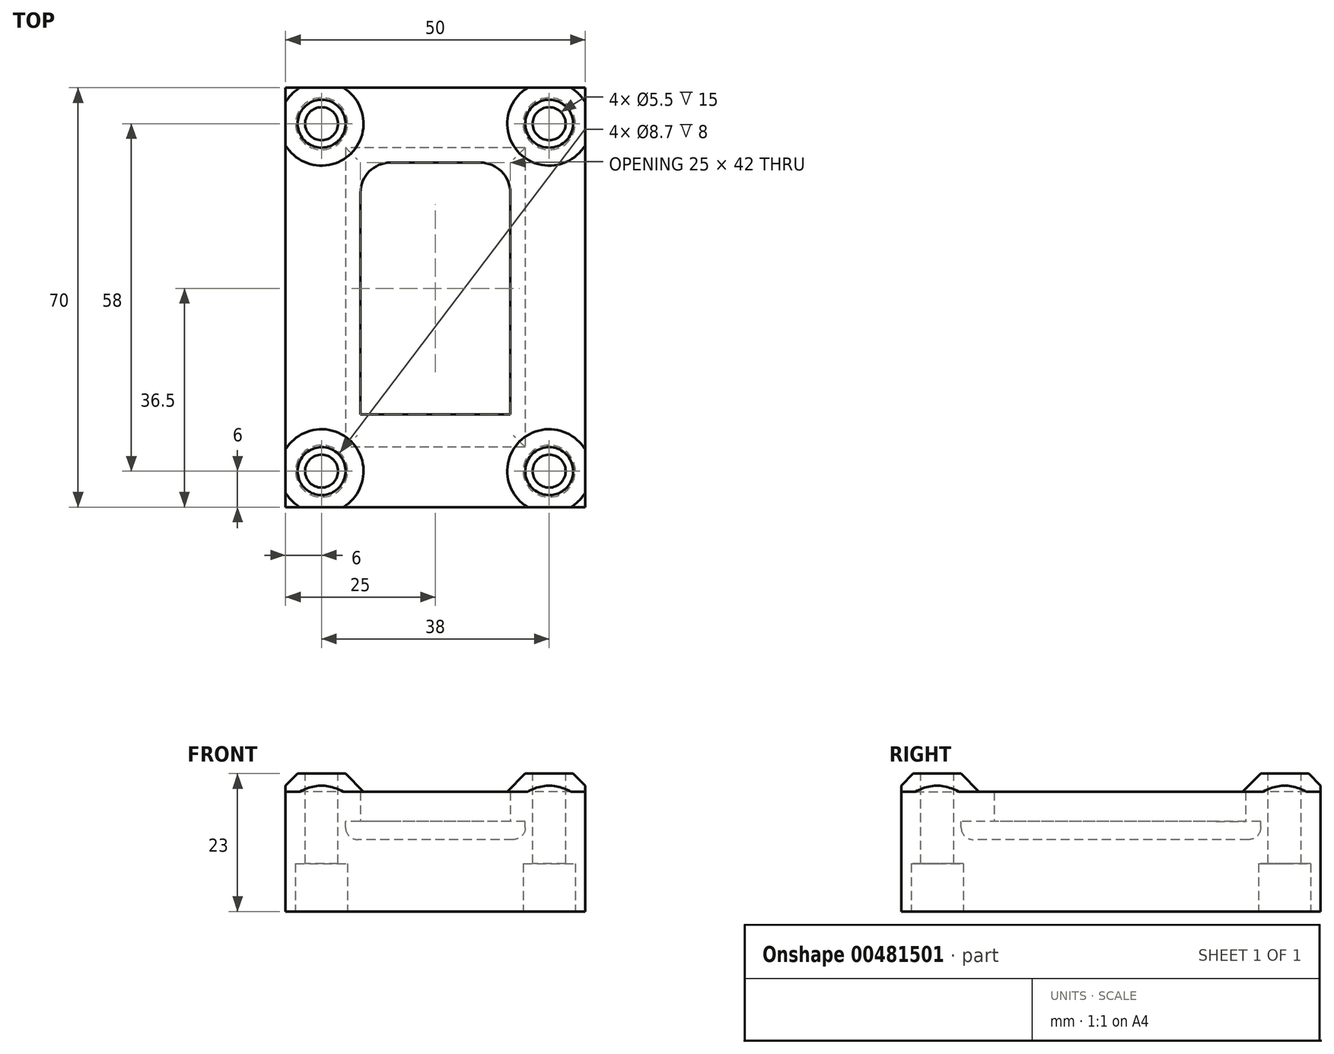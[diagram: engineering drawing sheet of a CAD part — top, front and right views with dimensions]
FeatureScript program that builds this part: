
annotation { "Feature Type Name" : "Feature", "Feature Type Description" : "" }
export const myFeature = defineFeature(function(context is Context, id is Id, definition is map)
    precondition{}
    {
        {
            var Q0;
            Q0=qCreatedBy(makeId("Top.planeOp"),FACE);
            var sketch = newSketch(context, id + "F0", { "sketchPlane" : qUnion([Q0])});
            skLineSegment(sketch, "E0.bottom", {"start": v(15, 25) * mm, "end": v(-15, 25) * mm});
            skLineSegment(sketch, "E0.top", {"start": v(15, -25) * mm, "end": v(-15, -25) * mm});
            skLineSegment(sketch, "E0.left", {"start": v(15, 25) * mm, "end": v(15, -25) * mm});
            skLineSegment(sketch, "E0.right", {"start": v(-15, 25) * mm, "end": v(-15, -25) * mm});
            skPoint(sketch, "E0.middle", {"position": v(0, 0) * mm});
            skLineSegment(sketch, "E1.bottom", {"start": v(25, 35) * mm, "end": v(-25, 35) * mm});
            skLineSegment(sketch, "E1.top", {"start": v(25, -35) * mm, "end": v(-25, -35) * mm});
            skLineSegment(sketch, "E1.left", {"start": v(25, 35) * mm, "end": v(25, -35) * mm});
            skLineSegment(sketch, "E1.right", {"start": v(-25, 35) * mm, "end": v(-25, -35) * mm});
            skLineSegment(sketch, "E2", {"start": v(-19, 35) * mm, "end": v(-19, 29) * mm});
            skCircle(sketch, "E3", {"center": v(-19, 29) * mm, "radius": 2.75 * mm});
            skLineSegment(sketch, "E4", {"start": v(-19, -35) * mm, "end": v(-19, -29) * mm});
            skLineSegment(sketch, "E5", {"start": v(-19, -29) * mm, "end": v(-25, -29) * mm});
            skCircle(sketch, "E6", {"center": v(-19, -29) * mm, "radius": 2.75 * mm});
            skLineSegment(sketch, "E7", {"start": v(25, -29) * mm, "end": v(19, -29) * mm});
            skCircle(sketch, "E8", {"center": v(19, -29) * mm, "radius": 2.75 * mm});
            skLineSegment(sketch, "E9", {"start": v(19, -29) * mm, "end": v(19, -35) * mm});
            skLineSegment(sketch, "E10", {"start": v(19, 35) * mm, "end": v(19, 29) * mm});
            skLineSegment(sketch, "E11", {"start": v(19, 29) * mm, "end": v(25, 29) * mm});
            skCircle(sketch, "E12", {"center": v(19, 29) * mm, "radius": 2.75 * mm});
            skSolve(sketch);
        }
        {
            var Q0;
            Q0=makeQuery(id+"F0.imprint","IMPRINT",FACE,{"disambiguationData":[TD([[makeQuery(id+"F0.imprint","IMPRINT",EDGE,{"derivedFrom":sQuery(id+"F0.wireOp",EDGE,"E0.bottom")}),-1.0]])]});
            var Q1;
            {var subQ1=sQuery(id+"F0.wireOp",EDGE,"E1.left");var subQ6=sQuery(id+"F0.wireOp",EDGE,"E1.bottom");var subQ9=makeQuery(id+"F0.imprint","INTERSECT",VERTEX,{"derivedFrom":[subQ6,subQ1]});Q1=makeQuery(id+"F0.imprint","IMPRINT",FACE,{"disambiguationData":[TD([[makeQuery(id+"F0.imprint","IMPRINT",EDGE,{"disambiguationData":[TD([[subQ9,-1.0]])],"derivedFrom":subQ6}),1.0]])]});}
            var Q2;
            {var subQ5=sQuery(id+"F0.wireOp",EDGE,"E1.left");var subQ7=sQuery(id+"F0.wireOp",EDGE,"E1.top");var subQ8=makeQuery(id+"F0.imprint","INTERSECT",VERTEX,{"derivedFrom":[subQ7,subQ5]});Q2=makeQuery(id+"F0.imprint","IMPRINT",FACE,{"disambiguationData":[TD([[makeQuery(id+"F0.imprint","IMPRINT",EDGE,{"disambiguationData":[TD([[subQ8,-1.0]])],"derivedFrom":subQ7}),-1.0]])]});}
            var Q3;
            {var subQ1=sQuery(id+"F0.wireOp",EDGE,"E1.top");var subQ6=sQuery(id+"F0.wireOp",EDGE,"E1.right");var subQ9=makeQuery(id+"F0.imprint","INTERSECT",VERTEX,{"derivedFrom":[subQ1,subQ6]});Q3=makeQuery(id+"F0.imprint","IMPRINT",FACE,{"disambiguationData":[TD([[makeQuery(id+"F0.imprint","IMPRINT",EDGE,{"disambiguationData":[TD([[subQ9,1.0]])],"derivedFrom":subQ1}),-1.0]])]});}
            var Q4;
            Q4=makeQuery(id+"F0.imprint","IMPRINT",FACE,{"disambiguationData":[TD([[makeQuery(id+"F0.imprint","IMPRINT",EDGE,{"derivedFrom":sQuery(id+"F0.wireOp",EDGE,"E0.bottom")}),1.0]])]});
            extrude(context, id + "F1", {"entities" : qUnion([Q0, Q1, Q2, Q3, Q4]), "oppositeDirection" : true, "depth" : 15 * mm});
        }
        {
            var Q0;
            Q0=makeQuery(id+"F1.opExtrude","CAP_FACE",FACE,{"disambiguationData":[OSD([sQuery(id+"F0.wireOp",EDGE,"E1.bottom"),sQuery(id+"F0.wireOp",EDGE,"E1.top"),sQuery(id+"F0.wireOp",EDGE,"E1.left"),sQuery(id+"F0.wireOp",EDGE,"E1.right"),sQuery(id+"F0.wireOp",EDGE,"E3"),sQuery(id+"F0.wireOp",EDGE,"E6"),sQuery(id+"F0.wireOp",EDGE,"E8"),sQuery(id+"F0.wireOp",EDGE,"E12")])],"isStart":false});
            var sketch = newSketch(context, id + "F2", { "sketchPlane" : qUnion([Q0])});
            skCircle(sketch, "E13", {"center": v(-19, 29) * mm, "radius": 4.35 * mm});
            skCircle(sketch, "E14", {"center": v(-19, -29) * mm, "radius": 4.35 * mm});
            skCircle(sketch, "E15", {"center": v(19, -29) * mm, "radius": 4.35 * mm});
            skCircle(sketch, "E16", {"center": v(19, 29) * mm, "radius": 4.35 * mm});
            skSolve(sketch);
        }
        {
            var Q0;
            Q0=makeQuery(id+"F2.imprint","IMPRINT",FACE,{"disambiguationData":[TD([[makeQuery(id+"F2.imprint","IMPRINT",EDGE,{"derivedFrom":sQuery(id+"F2.wireOp",EDGE,"E13")}),1.0]])]});
            var Q1;
            Q1=makeQuery(id+"F2.imprint","IMPRINT",FACE,{"disambiguationData":[TD([[makeQuery(id+"F2.imprint","IMPRINT",EDGE,{"derivedFrom":sQuery(id+"F2.wireOp",EDGE,"E16")}),1.0]])]});
            var Q2;
            Q2=makeQuery(id+"F2.imprint","IMPRINT",FACE,{"disambiguationData":[TD([[makeQuery(id+"F2.imprint","IMPRINT",EDGE,{"derivedFrom":sQuery(id+"F2.wireOp",EDGE,"E15")}),1.0]])]});
            var Q3;
            Q3=makeQuery(id+"F2.imprint","IMPRINT",FACE,{"disambiguationData":[TD([[makeQuery(id+"F2.imprint","IMPRINT",EDGE,{"derivedFrom":sQuery(id+"F2.wireOp",EDGE,"E14")}),1.0]])]});
            extrude(context, id + "F3", {"entities" : qUnion([Q0, Q1, Q2, Q3]), "operationType" : NewBodyOperationType.REMOVE, "oppositeDirection" : true, "depth" : 8 * mm});
        }
        {
            var Q0;
            Q0=makeQuery(id+"F0.imprint","IMPRINT",FACE,{"disambiguationData":[TD([[makeQuery(id+"F0.imprint","IMPRINT",EDGE,{"derivedFrom":sQuery(id+"F0.wireOp",EDGE,"E0.bottom")}),1.0]])]});
            extrude(context, id + "F4", {"entities" : qUnion([Q0]), "operationType" : NewBodyOperationType.REMOVE, "oppositeDirection" : true, "depth" : 3 * mm});
        }
        {
            var Q0;
            Q0=makeQuery(id+"F4.boolean.opBoolean","COPY",EDGE,{"derivedFrom":makeQuery(id+"F4.opExtrude","CAP_EDGE",EDGE,{"disambiguationData":[OSD([sQuery(id+"F0.wireOp",EDGE,"E0.bottom")])],"isStart":false})});
            var Q1;
            Q1=makeQuery(id+"F4.boolean.opBoolean","COPY",EDGE,{"derivedFrom":makeQuery(id+"F4.opExtrude","CAP_EDGE",EDGE,{"disambiguationData":[OSD([sQuery(id+"F0.wireOp",EDGE,"E0.left")])],"isStart":false})});
            var Q2;
            Q2=makeQuery(id+"F4.boolean.opBoolean","COPY",EDGE,{"derivedFrom":makeQuery(id+"F4.opExtrude","CAP_EDGE",EDGE,{"disambiguationData":[OSD([sQuery(id+"F0.wireOp",EDGE,"E0.right")])],"isStart":false})});
            var Q3;
            Q3=makeQuery(id+"F4.boolean.opBoolean","COPY",EDGE,{"derivedFrom":makeQuery(id+"F4.opExtrude","CAP_EDGE",EDGE,{"disambiguationData":[OSD([sQuery(id+"F0.wireOp",EDGE,"E0.top")])],"isStart":false})});
            fillet(context, id + "F5", {"entities" : qUnion([Q0, Q1, Q2, Q3]), "radius" : 2 * mm, "tangentPropagation" : true, "allowEdgeOverflow" : false});
        }
        {
            var Q0;
            Q0=makeQuery(id+"F1.opExtrude","CAP_FACE",FACE,{"disambiguationData":[OSD([sQuery(id+"F0.wireOp",EDGE,"E1.bottom"),sQuery(id+"F0.wireOp",EDGE,"E1.top"),sQuery(id+"F0.wireOp",EDGE,"E1.left"),sQuery(id+"F0.wireOp",EDGE,"E1.right"),sQuery(id+"F0.wireOp",EDGE,"E3"),sQuery(id+"F0.wireOp",EDGE,"E6"),sQuery(id+"F0.wireOp",EDGE,"E8"),sQuery(id+"F0.wireOp",EDGE,"E12")])],"isStart":true});
            var sketch = newSketch(context, id + "F6", { "sketchPlane" : qUnion([Q0])});
            skLineSegment(sketch, "E17.bottom", {"start": v(12.5, 22.5) * mm, "end": v(-12.5, 22.5) * mm});
            skLineSegment(sketch, "E17.top", {"start": v(12.5, -22.5) * mm, "end": v(-12.5, -22.5) * mm});
            skLineSegment(sketch, "E17.left", {"start": v(12.5, 22.5) * mm, "end": v(12.5, -22.5) * mm});
            skLineSegment(sketch, "E17.right", {"start": v(-12.5, 22.5) * mm, "end": v(-12.5, -22.5) * mm});
            skPoint(sketch, "E17.middle", {"position": v(0, 0) * mm});
            skLineSegment(sketch, "E18.bottom", {"start": v(25, 35) * mm, "end": v(-25, 35) * mm});
            skLineSegment(sketch, "E18.top", {"start": v(25, -35) * mm, "end": v(-25, -35) * mm});
            skLineSegment(sketch, "E18.left", {"start": v(25, 35) * mm, "end": v(25, -35) * mm});
            skLineSegment(sketch, "E18.right", {"start": v(-25, 35) * mm, "end": v(-25, -35) * mm});
            skCircle(sketch, "E19", {"center": v(19, -29) * mm, "radius": 2.75 * mm});
            skCircle(sketch, "E20", {"center": v(19, 29) * mm, "radius": 2.75 * mm});
            skCircle(sketch, "E21", {"center": v(-19, 29) * mm, "radius": 2.75 * mm});
            skCircle(sketch, "E22", {"center": v(-19, -29) * mm, "radius": 2.75 * mm});
            skCircle(sketch, "E23", {"center": v(-19, -29) * mm, "radius": 4 * mm});
            skCircle(sketch, "E24", {"center": v(19, -29) * mm, "radius": 4 * mm});
            skCircle(sketch, "E25", {"center": v(19, 29) * mm, "radius": 4 * mm});
            skCircle(sketch, "E26", {"center": v(-19, 29) * mm, "radius": 4 * mm});
            skSolve(sketch);
        }
        {
            var Q0;
            Q0=makeQuery(id+"F6.imprint","IMPRINT",FACE,{"disambiguationData":[TD([[makeQuery(id+"F6.imprint","IMPRINT",EDGE,{"derivedFrom":sQuery(id+"F6.wireOp",EDGE,"E18.bottom")}),1.0]])]});
            var Q1;
            Q1=makeQuery(id+"F6.imprint","IMPRINT",FACE,{"disambiguationData":[TD([[makeQuery(id+"F6.imprint","IMPRINT",EDGE,{"derivedFrom":sQuery(id+"F6.wireOp",EDGE,"E17.bottom")}),-1.0]])]});
            var Q2;
            Q2=makeQuery(id+"F6.imprint","IMPRINT",FACE,{"disambiguationData":[TD([[makeQuery(id+"F6.imprint","IMPRINT",EDGE,{"derivedFrom":sQuery(id+"F6.wireOp",EDGE,"E19")}),-1.0]])]});
            var Q3;
            Q3=makeQuery(id+"F6.imprint","IMPRINT",FACE,{"disambiguationData":[TD([[makeQuery(id+"F6.imprint","IMPRINT",EDGE,{"derivedFrom":sQuery(id+"F6.wireOp",EDGE,"E22")}),-1.0]])]});
            var Q4;
            Q4=makeQuery(id+"F6.imprint","IMPRINT",FACE,{"disambiguationData":[TD([[makeQuery(id+"F6.imprint","IMPRINT",EDGE,{"derivedFrom":sQuery(id+"F6.wireOp",EDGE,"E20")}),-1.0]])]});
            var Q5;
            Q5=makeQuery(id+"F6.imprint","IMPRINT",FACE,{"disambiguationData":[TD([[makeQuery(id+"F6.imprint","IMPRINT",EDGE,{"derivedFrom":sQuery(id+"F6.wireOp",EDGE,"E21")}),-1.0]])]});
            extrude(context, id + "F7", {"entities" : qUnion([Q0, Q1, Q2, Q3, Q4, Q5]), "depth" : 5 * mm});
        }
        {
            var Q0;
            Q0=makeQuery(id+"F6.imprint","IMPRINT",FACE,{"disambiguationData":[TD([[makeQuery(id+"F6.imprint","IMPRINT",EDGE,{"derivedFrom":sQuery(id+"F6.wireOp",EDGE,"E20")}),-1.0]])]});
            var Q1;
            Q1=makeQuery(id+"F6.imprint","IMPRINT",FACE,{"disambiguationData":[TD([[makeQuery(id+"F6.imprint","IMPRINT",EDGE,{"derivedFrom":sQuery(id+"F6.wireOp",EDGE,"E21")}),-1.0]])]});
            var Q2;
            Q2=makeQuery(id+"F6.imprint","IMPRINT",FACE,{"disambiguationData":[TD([[makeQuery(id+"F6.imprint","IMPRINT",EDGE,{"derivedFrom":sQuery(id+"F6.wireOp",EDGE,"E22")}),-1.0]])]});
            var Q3;
            Q3=makeQuery(id+"F6.imprint","IMPRINT",FACE,{"disambiguationData":[TD([[makeQuery(id+"F6.imprint","IMPRINT",EDGE,{"derivedFrom":sQuery(id+"F6.wireOp",EDGE,"E19")}),-1.0]])]});
            extrude(context, id + "F8", {"entities" : qUnion([Q0, Q1, Q2, Q3]), "operationType" : NewBodyOperationType.ADD, "depth" : 8 * mm});
        }
        {
            var Q0;
            Q0=makeQuery(id+"F7.opExtrude","SWEPT_FACE",FACE,{"disambiguationData":[OSD([sQuery(id+"F6.wireOp",EDGE,"E17.top")])]});
            extrude(context, id + "F9", {"entities" : qUnion([Q0]), "operationType" : NewBodyOperationType.ADD, "depth" : 3 * mm});
        }
        {
            var Q0;
            Q0=makeQuery(id+"F8.boolean.opBoolean","INTERSECT",EDGE,{"derivedFrom":[makeQuery(id+"F7.opExtrude","CAP_FACE",FACE,{"disambiguationData":[OSD([sQuery(id+"F6.wireOp",EDGE,"E17.bottom"),sQuery(id+"F6.wireOp",EDGE,"E17.top"),sQuery(id+"F6.wireOp",EDGE,"E17.left"),sQuery(id+"F6.wireOp",EDGE,"E17.right"),sQuery(id+"F6.wireOp",EDGE,"E18.bottom"),sQuery(id+"F6.wireOp",EDGE,"E18.top"),sQuery(id+"F6.wireOp",EDGE,"E18.left"),sQuery(id+"F6.wireOp",EDGE,"E18.right"),sQuery(id+"F6.wireOp",EDGE,"E19"),sQuery(id+"F6.wireOp",EDGE,"E20"),sQuery(id+"F6.wireOp",EDGE,"E21"),sQuery(id+"F6.wireOp",EDGE,"E22")])],"isStart":false}),makeQuery(id+"F8.opExtrude","SWEPT_FACE",FACE,{"disambiguationData":[OSD([sQuery(id+"F6.wireOp",EDGE,"E25")])]})]});
            var Q1;
            Q1=makeQuery(id+"F8.boolean.opBoolean","INTERSECT",EDGE,{"derivedFrom":[makeQuery(id+"F7.opExtrude","CAP_FACE",FACE,{"disambiguationData":[OSD([sQuery(id+"F6.wireOp",EDGE,"E17.bottom"),sQuery(id+"F6.wireOp",EDGE,"E17.top"),sQuery(id+"F6.wireOp",EDGE,"E17.left"),sQuery(id+"F6.wireOp",EDGE,"E17.right"),sQuery(id+"F6.wireOp",EDGE,"E18.bottom"),sQuery(id+"F6.wireOp",EDGE,"E18.top"),sQuery(id+"F6.wireOp",EDGE,"E18.left"),sQuery(id+"F6.wireOp",EDGE,"E18.right"),sQuery(id+"F6.wireOp",EDGE,"E19"),sQuery(id+"F6.wireOp",EDGE,"E20"),sQuery(id+"F6.wireOp",EDGE,"E21"),sQuery(id+"F6.wireOp",EDGE,"E22")])],"isStart":false}),makeQuery(id+"F8.opExtrude","SWEPT_FACE",FACE,{"disambiguationData":[OSD([sQuery(id+"F6.wireOp",EDGE,"E24")])]})]});
            var Q2;
            Q2=makeQuery(id+"F8.boolean.opBoolean","INTERSECT",EDGE,{"derivedFrom":[makeQuery(id+"F7.opExtrude","CAP_FACE",FACE,{"disambiguationData":[OSD([sQuery(id+"F6.wireOp",EDGE,"E17.bottom"),sQuery(id+"F6.wireOp",EDGE,"E17.top"),sQuery(id+"F6.wireOp",EDGE,"E17.left"),sQuery(id+"F6.wireOp",EDGE,"E17.right"),sQuery(id+"F6.wireOp",EDGE,"E18.bottom"),sQuery(id+"F6.wireOp",EDGE,"E18.top"),sQuery(id+"F6.wireOp",EDGE,"E18.left"),sQuery(id+"F6.wireOp",EDGE,"E18.right"),sQuery(id+"F6.wireOp",EDGE,"E19"),sQuery(id+"F6.wireOp",EDGE,"E20"),sQuery(id+"F6.wireOp",EDGE,"E21"),sQuery(id+"F6.wireOp",EDGE,"E22")])],"isStart":false}),makeQuery(id+"F8.opExtrude","SWEPT_FACE",FACE,{"disambiguationData":[OSD([sQuery(id+"F6.wireOp",EDGE,"E23")])]})]});
            var Q3;
            Q3=makeQuery(id+"F8.boolean.opBoolean","INTERSECT",EDGE,{"derivedFrom":[makeQuery(id+"F7.opExtrude","CAP_FACE",FACE,{"disambiguationData":[OSD([sQuery(id+"F6.wireOp",EDGE,"E17.bottom"),sQuery(id+"F6.wireOp",EDGE,"E17.top"),sQuery(id+"F6.wireOp",EDGE,"E17.left"),sQuery(id+"F6.wireOp",EDGE,"E17.right"),sQuery(id+"F6.wireOp",EDGE,"E18.bottom"),sQuery(id+"F6.wireOp",EDGE,"E18.top"),sQuery(id+"F6.wireOp",EDGE,"E18.left"),sQuery(id+"F6.wireOp",EDGE,"E18.right"),sQuery(id+"F6.wireOp",EDGE,"E19"),sQuery(id+"F6.wireOp",EDGE,"E20"),sQuery(id+"F6.wireOp",EDGE,"E21"),sQuery(id+"F6.wireOp",EDGE,"E22")])],"isStart":false}),makeQuery(id+"F8.opExtrude","SWEPT_FACE",FACE,{"disambiguationData":[OSD([sQuery(id+"F6.wireOp",EDGE,"E26")])]})]});
            chamfer(context, id + "F10", {"entities" : qUnion([Q0, Q1, Q2, Q3]), "width" : 3 * mm, "tangentPropagation" : true});
        }
        {
            var Q0;
            Q0=makeQuery(id+"F9.opExtrude","CAP_EDGE",EDGE,{"disambiguationData":[OSD([sQuery(id+"F6.wireOp",EDGE,"E17.top"),sQuery(id+"F6.wireOp",EDGE,"E17.right")])],"isStart":false});
            var Q1;
            Q1=makeQuery(id+"F9.opExtrude","CAP_EDGE",EDGE,{"disambiguationData":[OSD([sQuery(id+"F6.wireOp",EDGE,"E17.top"),sQuery(id+"F6.wireOp",EDGE,"E17.left")])],"isStart":false});
            var Q2;
            Q2=makeQuery(id+"F7.opExtrude","SWEPT_EDGE",EDGE,{"disambiguationData":[OSD([sQuery(id+"F6.wireOp",EDGE,"E17.bottom"),sQuery(id+"F6.wireOp",EDGE,"E17.right")])]});
            var Q3;
            Q3=makeQuery(id+"F7.opExtrude","SWEPT_EDGE",EDGE,{"disambiguationData":[OSD([sQuery(id+"F6.wireOp",EDGE,"E17.bottom"),sQuery(id+"F6.wireOp",EDGE,"E17.left")])]});
            fillet(context, id + "F11", {"entities" : qUnion([Q0, Q1, Q2, Q3]), "radius" : 5 * mm, "tangentPropagation" : true, "allowEdgeOverflow" : false});
        }
    });
